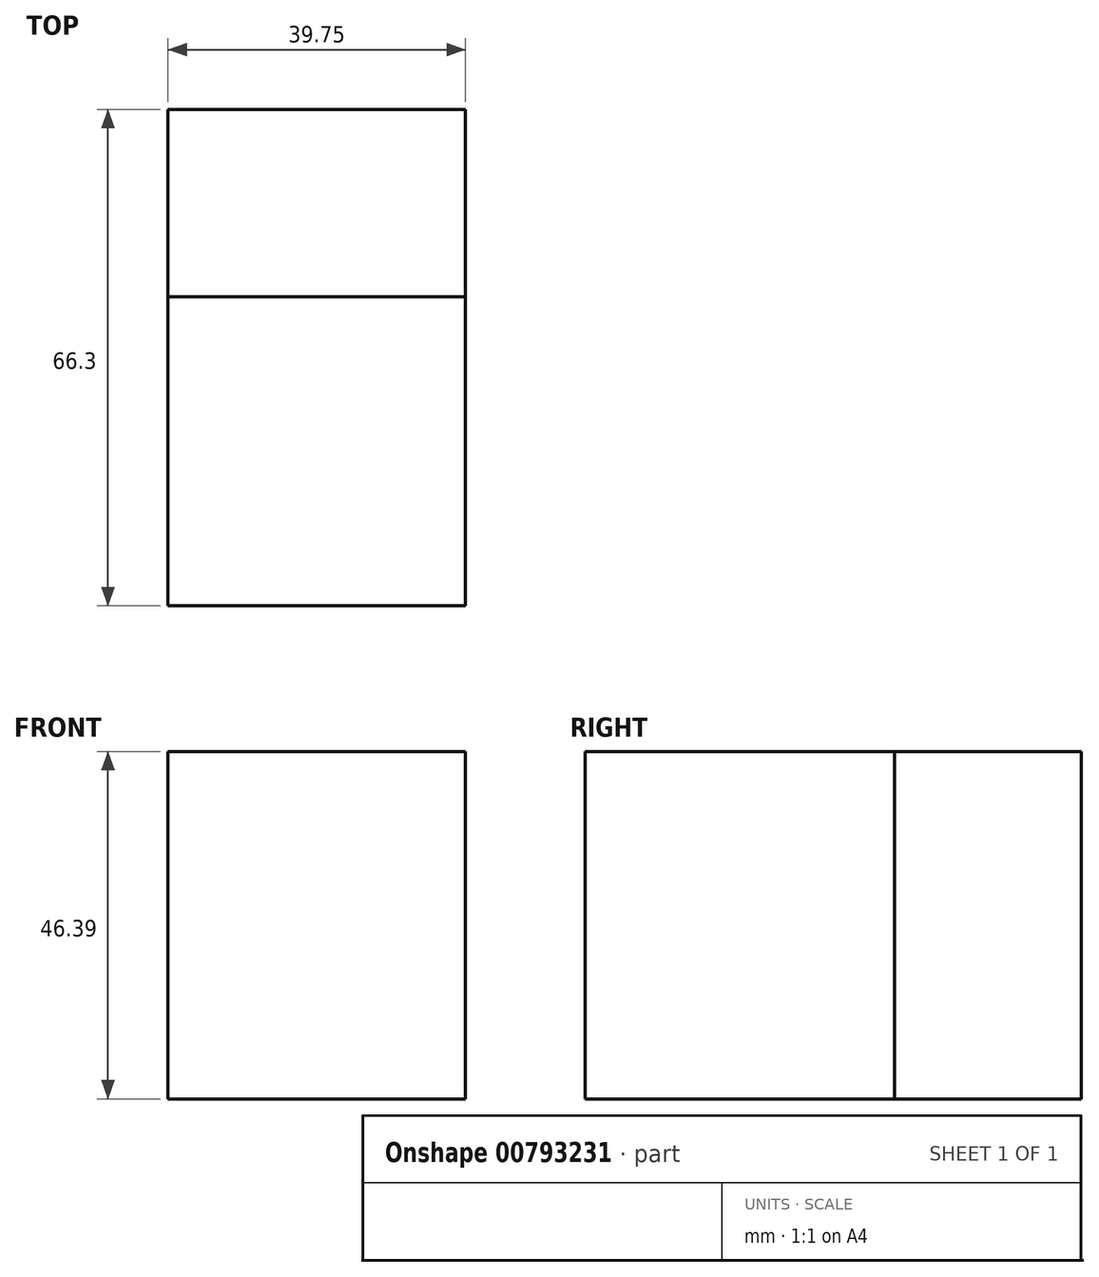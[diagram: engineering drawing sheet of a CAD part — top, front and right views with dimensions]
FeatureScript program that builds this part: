
annotation { "Feature Type Name" : "Feature", "Feature Type Description" : "" }
export const myFeature = defineFeature(function(context is Context, id is Id, definition is map)
    precondition{}
    {
        {
            var Q0;
            Q0=qCreatedBy(makeId("Front.planeOp"),FACE);
            var sketch = newSketch(context, id + "F0", { "sketchPlane" : qUnion([Q0])});
            skLineSegment(sketch, "E0.bottom", {"start": v(-154.45, 30.67) * mm, "end": v(-114.7, 30.67) * mm});
            skLineSegment(sketch, "E0.top", {"start": v(-154.45, -15.72) * mm, "end": v(-114.7, -15.72) * mm});
            skLineSegment(sketch, "E0.left", {"start": v(-154.45, 30.67) * mm, "end": v(-154.45, -15.72) * mm});
            skLineSegment(sketch, "E0.right", {"start": v(-114.7, 30.67) * mm, "end": v(-114.7, -15.72) * mm});
            skSolve(sketch);
        }
        {
            var Q0;
            Q0 = qSketchRegion(id + "F0", true);
            extrude(context, id + "F1", {"entities" : qUnion([Q0]), "depth" : 25 * mm, "offsetDistance" : 25 * mm});
        }
        {
            var Q0;
            Q0=makeQuery(id+"F1.opExtrude","CAP_FACE",FACE,{"disambiguationData":[OSD([sQuery(id+"F0.wireOp",EDGE,"E0.bottom"),sQuery(id+"F0.wireOp",EDGE,"E0.top"),sQuery(id+"F0.wireOp",EDGE,"E0.left"),sQuery(id+"F0.wireOp",EDGE,"E0.right")])],"isStart":false});
            extrude(context, id + "F2", {"entities" : qUnion([Q0]), "depth" : 41.3 * mm, "offsetDistance" : 25 * mm});
        }
    });
